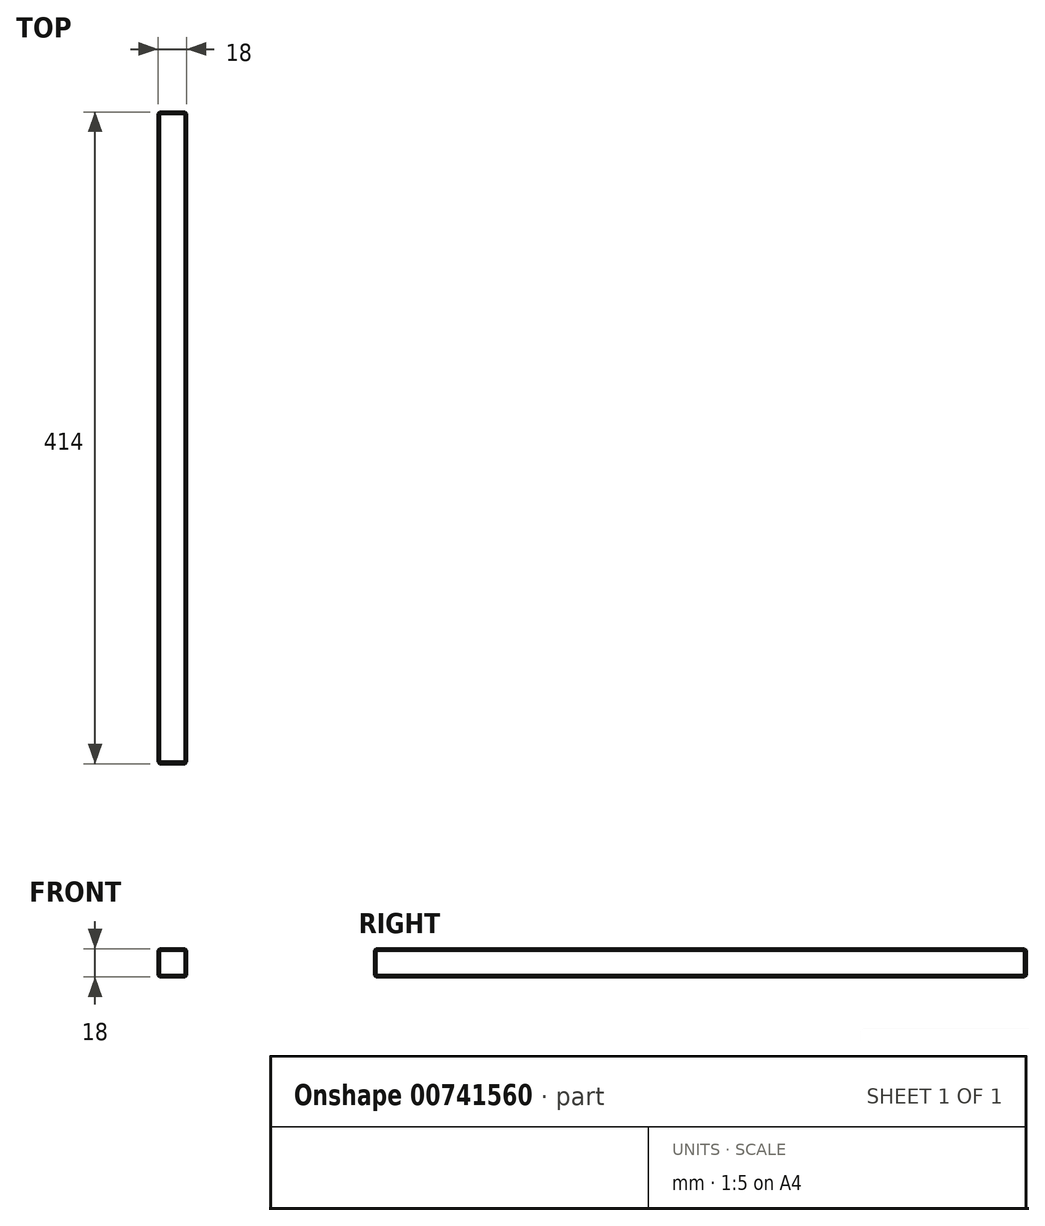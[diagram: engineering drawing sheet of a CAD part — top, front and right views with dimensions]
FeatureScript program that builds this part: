
annotation { "Feature Type Name" : "Feature", "Feature Type Description" : "" }
export const myFeature = defineFeature(function(context is Context, id is Id, definition is map)
    precondition{}
    {
        {
            var Q0;
            Q0=qCreatedBy(makeId("Front.planeOp"),FACE);
            var sketch = newSketch(context, id + "F0", { "sketchPlane" : qUnion([Q0])});
            skLineSegment(sketch, "E0.bottom", {"start": v(-9, -9) * mm, "end": v(9, -9) * mm});
            skLineSegment(sketch, "E0.top", {"start": v(-9, 9) * mm, "end": v(9, 9) * mm});
            skLineSegment(sketch, "E0.left", {"start": v(-9, -9) * mm, "end": v(-9, 9) * mm});
            skLineSegment(sketch, "E0.right", {"start": v(9, -9) * mm, "end": v(9, 9) * mm});
            skPoint(sketch, "E0.middle", {"position": v(0, 0) * mm});
            skSolve(sketch);
        }
        {
            var Q0;
            Q0 = qSketchRegion(id + "F0", true);
            extrude(context, id + "F1", {"entities" : qUnion([Q0]), "endBound" : BoundingType.SYMMETRIC, "depth" : 414 * mm, "offsetDistance" : 25 * mm});
        }
        {
            var Q0;
            Q0=makeQuery(id+"F1.opExtrude","SWEPT_EDGE",EDGE,{"disambiguationData":[OSD([sQuery(id+"F0.wireOp",EDGE,"E0.top"),sQuery(id+"F0.wireOp",EDGE,"E0.right")])]});
            var Q1;
            Q1=makeQuery(id+"F1.opExtrude","SWEPT_EDGE",EDGE,{"disambiguationData":[OSD([sQuery(id+"F0.wireOp",EDGE,"E0.top"),sQuery(id+"F0.wireOp",EDGE,"E0.left")])]});
            var Q2;
            Q2=makeQuery(id+"F1.opExtrude","SWEPT_EDGE",EDGE,{"disambiguationData":[OSD([sQuery(id+"F0.wireOp",EDGE,"E0.bottom"),sQuery(id+"F0.wireOp",EDGE,"E0.right")])]});
            var Q3;
            Q3=makeQuery(id+"F1.opExtrude","CAP_EDGE",EDGE,{"disambiguationData":[OSD([sQuery(id+"F0.wireOp",EDGE,"E0.bottom")])],"isStart":false});
            var Q4;
            Q4=makeQuery(id+"F1.opExtrude","SWEPT_EDGE",EDGE,{"disambiguationData":[OSD([sQuery(id+"F0.wireOp",EDGE,"E0.bottom"),sQuery(id+"F0.wireOp",EDGE,"E0.left")])]});
            var Q5;
            Q5=makeQuery(id+"F1.opExtrude","CAP_EDGE",EDGE,{"disambiguationData":[OSD([sQuery(id+"F0.wireOp",EDGE,"E0.bottom")])],"isStart":true});
            var Q6;
            Q6=makeQuery(id+"F1.opExtrude","CAP_EDGE",EDGE,{"disambiguationData":[OSD([sQuery(id+"F0.wireOp",EDGE,"E0.top")])],"isStart":true});
            var Q7;
            Q7=makeQuery(id+"F1.opExtrude","CAP_EDGE",EDGE,{"disambiguationData":[OSD([sQuery(id+"F0.wireOp",EDGE,"E0.top")])],"isStart":false});
            var Q8;
            Q8=makeQuery(id+"F1.opExtrude","CAP_EDGE",EDGE,{"disambiguationData":[OSD([sQuery(id+"F0.wireOp",EDGE,"E0.left")])],"isStart":true});
            var Q9;
            Q9=makeQuery(id+"F1.opExtrude","CAP_EDGE",EDGE,{"disambiguationData":[OSD([sQuery(id+"F0.wireOp",EDGE,"E0.left")])],"isStart":false});
            var Q10;
            Q10=makeQuery(id+"F1.opExtrude","CAP_EDGE",EDGE,{"disambiguationData":[OSD([sQuery(id+"F0.wireOp",EDGE,"E0.right")])],"isStart":true});
            var Q11;
            Q11=makeQuery(id+"F1.opExtrude","CAP_EDGE",EDGE,{"disambiguationData":[OSD([sQuery(id+"F0.wireOp",EDGE,"E0.right")])],"isStart":false});
            chamfer(context, id + "F2", {"entities" : qUnion([Q0, Q1, Q2, Q3, Q4, Q5, Q6, Q7, Q8, Q9, Q10, Q11]), "width" : 1 * mm, "tangentPropagation" : true});
        }
    });
